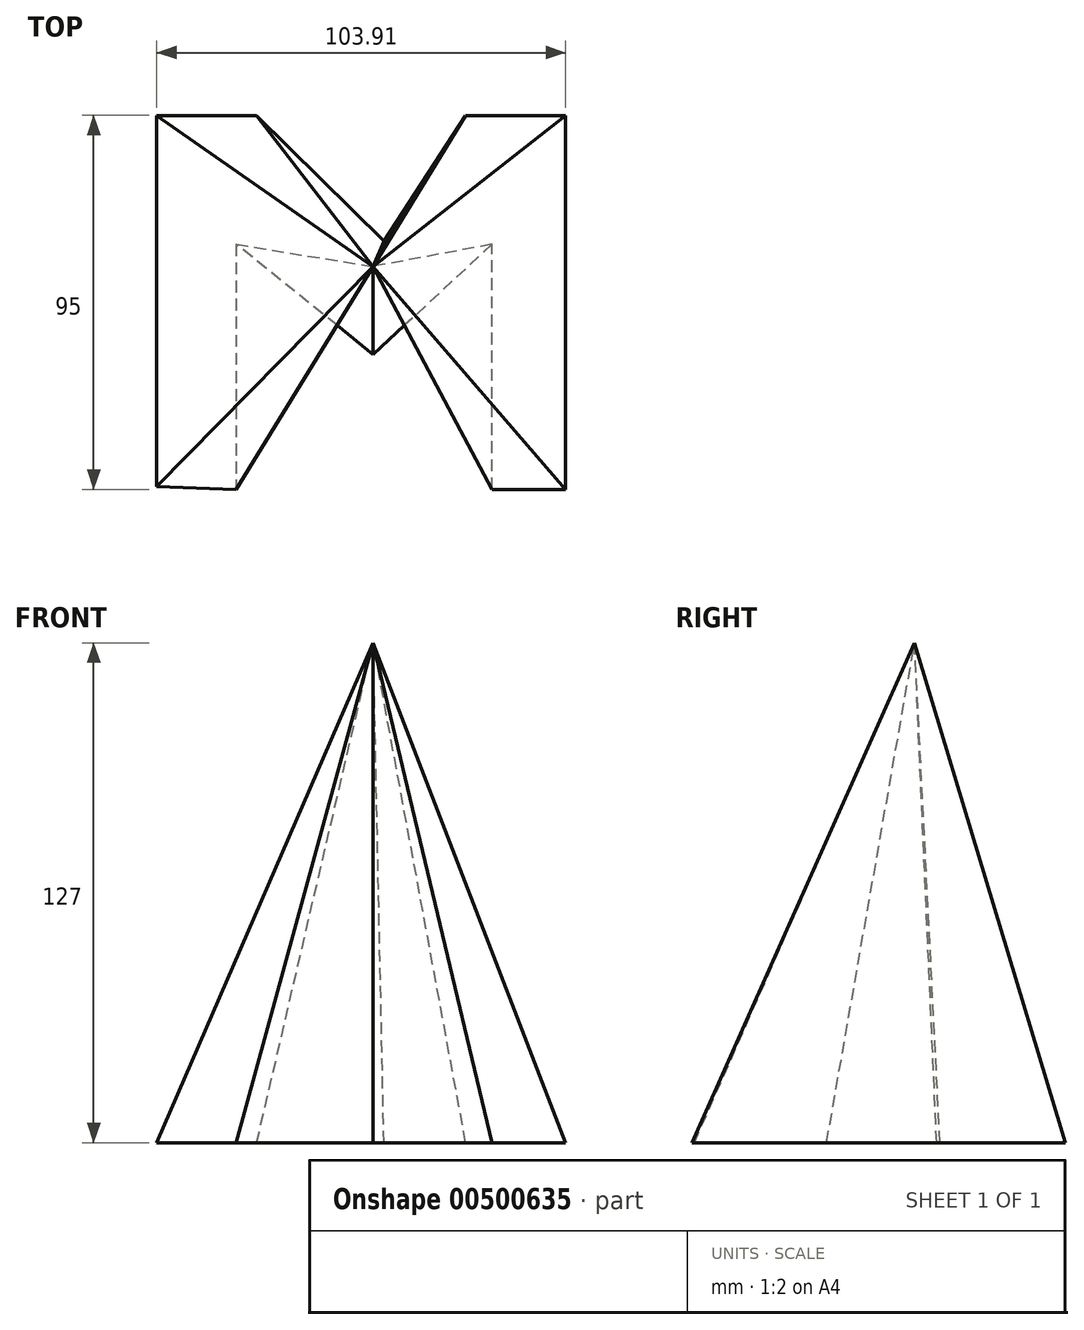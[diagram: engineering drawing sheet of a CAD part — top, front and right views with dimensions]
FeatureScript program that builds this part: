
annotation { "Feature Type Name" : "Feature", "Feature Type Description" : "" }
export const myFeature = defineFeature(function(context is Context, id is Id, definition is map)
    precondition{}
    {
        {
            var Q0;
            Q0=qCreatedBy(makeId("Top.planeOp"),FACE);
            var sketch = newSketch(context, id + "F0", { "sketchPlane" : qUnion([Q0])});
            skLineSegment(sketch, "E0", {"start": v(-55, 43.75) * mm, "end": v(-55, -50.6) * mm});
            skLineSegment(sketch, "E1", {"start": v(-55, 43.75) * mm, "end": v(-29.6, 43.75) * mm});
            skLineSegment(sketch, "E2", {"start": v(2.73, 11.82) * mm, "end": v(23.52, 43.75) * mm});
            skLineSegment(sketch, "E3", {"start": v(23.52, 43.75) * mm, "end": v(48.92, 43.75) * mm});
            skLineSegment(sketch, "E4", {"start": v(48.92, 43.75) * mm, "end": v(48.92, -51.25) * mm});
            skLineSegment(sketch, "E5", {"start": v(48.92, -51.25) * mm, "end": v(30.18, -51.25) * mm});
            skLineSegment(sketch, "E6", {"start": v(30.18, -51.25) * mm, "end": v(30.18, 10.99) * mm});
            skLineSegment(sketch, "E7", {"start": v(30.18, 10.99) * mm, "end": v(0, -16.97) * mm});
            skLineSegment(sketch, "E8", {"start": v(0, -16.97) * mm, "end": v(-34.78, 10.99) * mm});
            skLineSegment(sketch, "E9", {"start": v(-34.78, 10.99) * mm, "end": v(-34.78, -51.25) * mm});
            skLineSegment(sketch, "E10", {"start": v(-34.78, -51.25) * mm, "end": v(-55, -50.6) * mm});
            skLineSegment(sketch, "E11", {"start": v(-29.6, 43.75) * mm, "end": v(2.73, 11.82) * mm});
            skSolve(sketch);
        }
        {
            var Q0;
            Q0=qCreatedBy(makeId("Top.planeOp"),FACE);
            cPlane(context, id + "F1", {"entities" : qUnion([Q0]), "cplaneType" : CPlaneType.OFFSET, "offset" : 127 * mm, "width" : 152.4 * mm, "height" : 152.4 * mm});
        }
        {
            var Q0;
            Q0=qCreatedBy(id+"F1.planeOp",FACE);
            var sketch = newSketch(context, id + "F2", { "sketchPlane" : qUnion([Q0])});
            skPoint(sketch, "E12", {"position": v(0, 5.38) * mm});
            skSolve(sketch);
        }
        {
            var Q0;
            Q0 = qSketchRegion(id + "F0", true);
            var Q1;
            Q1=sQuery(id+"F2.wireOp",VERTEX,"E12");
            loft(context, id + "F3", {"sheetProfilesArray" : [{ "sheetProfileEntities" : qUnion([Q0]) }, { "sheetProfileEntities" : qUnion([Q1]) }]});
        }
    });
